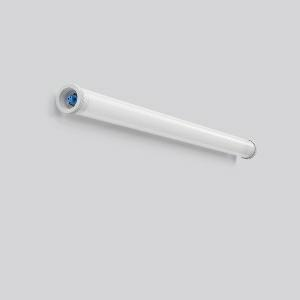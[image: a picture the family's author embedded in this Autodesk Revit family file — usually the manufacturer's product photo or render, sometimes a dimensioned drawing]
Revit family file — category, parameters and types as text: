
# Revit family: planox_tube_601071_002_1_730_3750
name_source: partatom
category: Lighting Fixtures
units: mm (PartAtom-declared; Revit-internal decimal feet)

## family parameters
Cut with Voids When Loaded = No
Host = Face
Light Source = No
Part Type = Normal
Room Calculation Point = No
Round Connector Dimension = Use Diameter
Shared = No

## types (1)
- PLANOX TUBE (1 x LED Modul 840, 5350 lm, 4000)
    Apparent Load = 39 VA
    CIE Flux Codes = 42 71 89 90 100
    Color Rendering = 80
    Color Temperature = 4000
    Default Elevation = 1800 mm
    Description = Series: PLANOX TUBE
Robust protective tube luminaire for tough requirements. Rack made of sheet steel, white powder coated. End caps made of plastic (polyamide) grey. Diffuser made of plastic (polycarbonate), opal, shockproof. Symmetrical light distribution. Homogeneous light distribution. With accessories for wall, ceiling or pendant mounting. Driver integrated. Easy installation with the Plug+Play Wieland RST CLASSIC plug-in system. Luminaire with integrated through-wiring for series connection of further luminaires by two Wieland RST Classic plug connectors (plug and socket). With Casambi smart+free Bluetooth control for wireless network and operation using Android / iOS devices, free app available for download. Accessories for electrical connection must be ordered separately. Mounting set must be ordered separately. Luminaire with limited surface temperature in accordance with EN 60598-2-24 for use in environments in which a deposit of conductive dust on the luminaire can be expected. Qualified for use in the food and drink industry. Suitable for lighting in public car parks and public off-street parking spaces according to DIN 67528. Environmentally friendly and resource-saving due to replaceable components. 
Colour: white
Diameter: 78 mm
Length: 1280 mm
Lamp: LED
Socket: without socket
Colour temperature: 4000K
Colour rendering index (CRI): 83
System power: 39 W
Rated luminous flux: 5350 lm
Luminous efficiency: 137 lm/W
Control gear: Dimmable Bluetooth converter
Protection class: I
Type of protection: IP 67
    Height = 0 mm  [stored 0 ft]
    Lamp = 1 x LED Modul 840
    Lamp Light Flux = 5350 lm
    Lamp count = 1
    Length = 1280 mm
    Lifetime = 50000 h
    Luminous efficacy = 137 lm/W
    Manufacturer = RZB
    ModVariant = No
    Model = 601071.002.1.730
    Mounting Place = Ceiling
    Mounting Type = Surface mounted
    Number of Poles = 1
    OnlyDefault = Yes
    Power Factor = 1
    Product Name = PLANOX TUBE
    Product group = Surface mounted luminaires for moist/humid enviroments
    ProductGroupID = 308
    Protection Class = Protection class I
    Protection Degree = Degree of protection
    RLX_Detail_Level = 1
    RLX_Emergency_Light_Flux = 0 lm
    RLX_Emergency_Type = 0
    RLX_Emergency_Type_DB = No
    RlxData = <blob elided: 34149 chars, md5=6edfeae8>
    Socket = socket
    Standby Power = 0 W
    System Light Flux = 5350 lm
    System Power = 39 W
    Type Comments = Product without accessories
    Type Image = 601071.002.jpg
    URL = http://relux.com
    VarID = ---
    Voltage = 0 V
    Weight = 0.00 kg
    Width = 0 mm  [stored 0 ft]

note: [stored X ft] marks values corroborated as IEEE doubles in the binary element streams (Revit-internal decimal feet)

## geometry (parser evidence)
native form markers: Blend x4, Sweep x14
no freeform markers — native parametric forms only
